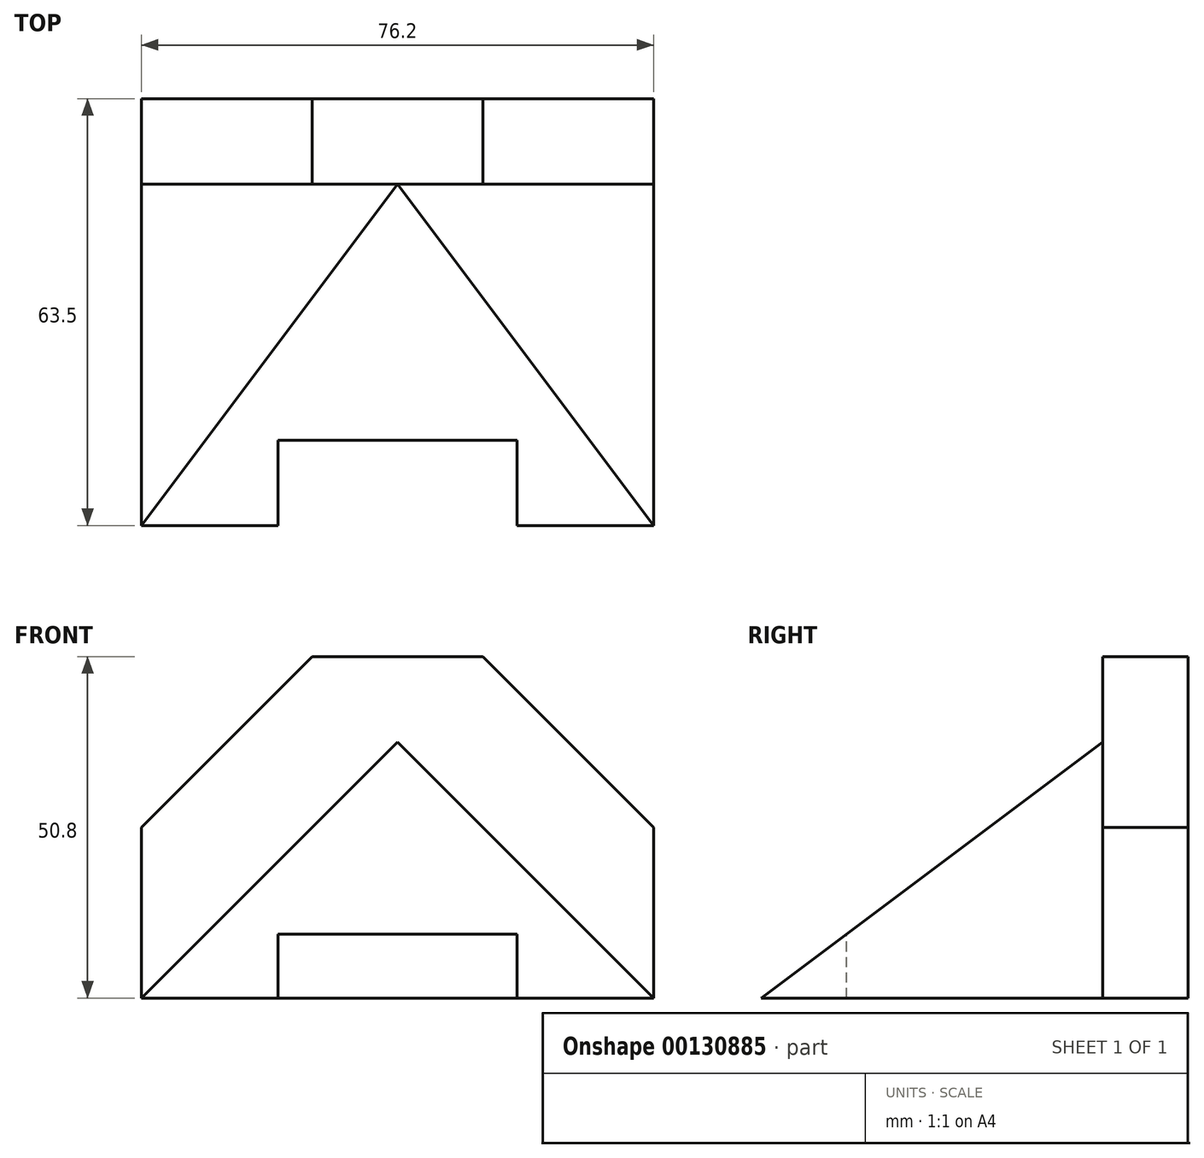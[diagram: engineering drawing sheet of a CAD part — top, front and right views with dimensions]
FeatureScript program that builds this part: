
annotation { "Feature Type Name" : "Feature", "Feature Type Description" : "" }
export const myFeature = defineFeature(function(context is Context, id is Id, definition is map)
    precondition{}
    {
        {
            var Q0;
            Q0=qCreatedBy(makeId("Front.planeOp"),FACE);
            var sketch = newSketch(context, id + "F0", { "sketchPlane" : qUnion([Q0])});
            skLineSegment(sketch, "E0", {"start": v(0, 0) * mm, "end": v(0, 25.4) * mm});
            skLineSegment(sketch, "E1", {"start": v(0, 25.4) * mm, "end": v(25.4, 50.8) * mm});
            skLineSegment(sketch, "E2", {"start": v(25.4, 50.8) * mm, "end": v(50.8, 50.8) * mm});
            skLineSegment(sketch, "E3", {"start": v(50.8, 50.8) * mm, "end": v(76.2, 25.4) * mm});
            skLineSegment(sketch, "E4", {"start": v(76.2, 25.4) * mm, "end": v(76.2, 0) * mm});
            skLineSegment(sketch, "E5", {"start": v(76.2, 0) * mm, "end": v(0, 0) * mm});
            skLineSegment(sketch, "E6", {"start": v(0, 0) * mm, "end": v(38.1, 38.1) * mm});
            skLineSegment(sketch, "E7", {"start": v(38.1, 38.1) * mm, "end": v(76.2, 0) * mm});
            skLineSegment(sketch, "E8", {"start": v(20.32, 0) * mm, "end": v(20.32, 12.7) * mm});
            skLineSegment(sketch, "E9", {"start": v(20.32, 12.7) * mm, "end": v(55.88, 12.7) * mm});
            skLineSegment(sketch, "E10", {"start": v(55.88, 12.7) * mm, "end": v(55.88, 0) * mm});
            skLineSegment(sketch, "E11", {"start": v(55.88, 0) * mm, "end": v(20.32, 0) * mm});
            skLineSegment(sketch, "E12", {"start": v(0, 0) * mm, "end": v(20.32, 0) * mm});
            skLineSegment(sketch, "E13", {"start": v(55.88, 0) * mm, "end": v(76.2, 0) * mm});
            skSolve(sketch);
        }
        {
            var Q0;
            Q0=makeQuery(id+"F0.imprint","IMPRINT",FACE,{"disambiguationData":[TD([[makeQuery(id+"F0.imprint","IMPRINT",EDGE,{"derivedFrom":sQuery(id+"F0.wireOp",EDGE,"E8")}),-1.0]])]});
            extrude(context, id + "F1", {"entities" : qUnion([Q0]), "depth" : 38.1 * mm});
        }
        {
            var Q0;
            Q0=makeQuery(id+"F0.imprint","IMPRINT",FACE,{"disambiguationData":[TD([[makeQuery(id+"F0.imprint","IMPRINT",EDGE,{"derivedFrom":sQuery(id+"F0.wireOp",EDGE,"E6")}),-1.0]])]});
            extrude(context, id + "F2", {"entities" : qUnion([Q0]), "operationType" : NewBodyOperationType.ADD, "depth" : 50.8 * mm});
        }
        {
            var Q0;
            Q0=qCreatedBy(makeId("Right.planeOp"),FACE);
            var sketch = newSketch(context, id + "F3", { "sketchPlane" : qUnion([Q0])});
            skLineSegment(sketch, "E14", {"start": v(0, 38.1) * mm, "end": v(-50.8, 0) * mm});
            skLineSegment(sketch, "E15", {"start": v(-50.8, 0) * mm, "end": v(-50.8, 38.1) * mm});
            skLineSegment(sketch, "E16", {"start": v(-50.8, 38.1) * mm, "end": v(0, 38.1) * mm});
            skSolve(sketch);
        }
        {
            var Q0;
            Q0=makeQuery(id+"F3.imprint","IMPRINT",FACE,{"disambiguationData":[TD([[makeQuery(id+"F3.imprint","IMPRINT",EDGE,{"derivedFrom":sQuery(id+"F3.wireOp",EDGE,"E14")}),-1.0]])]});
            extrude(context, id + "F4", {"entities" : qUnion([Q0]), "operationType" : NewBodyOperationType.REMOVE, "endBound" : BoundingType.THROUGH_ALL, "depth" : 25.4 * mm});
        }
        {
            var Q0;
            Q0=makeQuery(id+"F0.imprint","IMPRINT",FACE,{"disambiguationData":[TD([[makeQuery(id+"F0.imprint","IMPRINT",EDGE,{"derivedFrom":sQuery(id+"F0.wireOp",EDGE,"E0")}),-1.0]])]});
            extrude(context, id + "F5", {"entities" : qUnion([Q0]), "operationType" : NewBodyOperationType.ADD, "oppositeDirection" : true, "depth" : 12.7 * mm});
        }
        {
            var Q0;
            Q0=makeQuery(id+"F0.imprint","IMPRINT",FACE,{"disambiguationData":[TD([[makeQuery(id+"F0.imprint","IMPRINT",EDGE,{"derivedFrom":sQuery(id+"F0.wireOp",EDGE,"E8")}),-1.0]])]});
            var Q1;
            Q1=makeQuery(id+"F0.imprint","IMPRINT",FACE,{"disambiguationData":[TD([[makeQuery(id+"F0.imprint","IMPRINT",EDGE,{"derivedFrom":sQuery(id+"F0.wireOp",EDGE,"E0")}),-1.0]])]});
            var Q2;
            Q2=makeQuery(id+"F0.imprint","IMPRINT",FACE,{"disambiguationData":[TD([[makeQuery(id+"F0.imprint","IMPRINT",EDGE,{"derivedFrom":sQuery(id+"F0.wireOp",EDGE,"E6")}),-1.0]])]});
            extrude(context, id + "F6", {"entities" : qUnion([Q0, Q1, Q2]), "operationType" : NewBodyOperationType.ADD, "oppositeDirection" : true, "depth" : 12.7 * mm});
        }
    });
